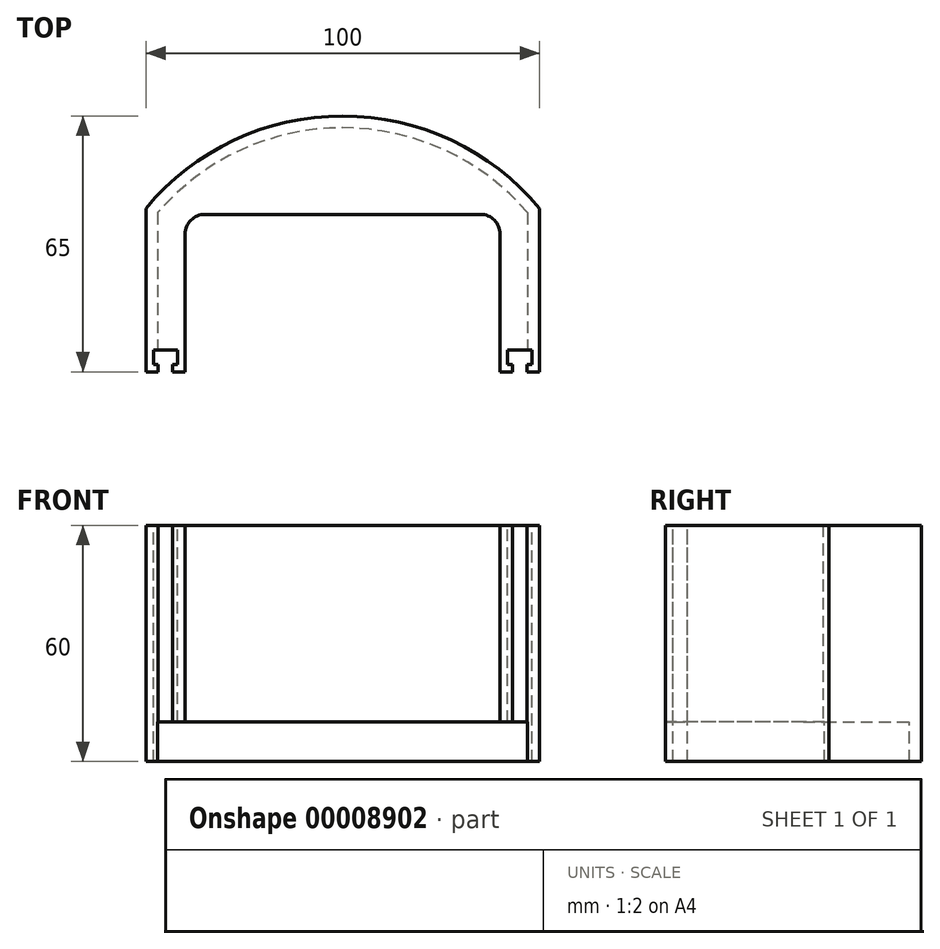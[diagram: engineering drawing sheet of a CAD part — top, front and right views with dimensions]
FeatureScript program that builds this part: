
annotation { "Feature Type Name" : "Feature", "Feature Type Description" : "" }
export const myFeature = defineFeature(function(context is Context, id is Id, definition is map)
    precondition{}
    {
        {
            var Q0;
            Q0=qCreatedBy(makeId("Top.planeOp"),FACE);
            var sketch = newSketch(context, id + "F0", { "sketchPlane" : qUnion([Q0])});
            skLineSegment(sketch, "E0", {"start": v(0, 0) * mm, "end": v(-40, 0) * mm});
            skLineSegment(sketch, "E1", {"start": v(0, 0) * mm, "end": v(40, 0) * mm});
            skLineSegment(sketch, "E2", {"start": v(0, 35) * mm, "end": v(0, 0) * mm});
            skLineSegment(sketch, "E3", {"start": v(-40, 0) * mm, "end": v(-43.59, 0) * mm});
            skLineSegment(sketch, "E4", {"start": v(40, 0) * mm, "end": v(43.59, 0) * mm});
            skLineSegment(sketch, "E5", {"start": v(-43.59, 0) * mm, "end": v(-50, 0) * mm});
            skLineSegment(sketch, "E6", {"start": v(43.59, 0) * mm, "end": v(50, 0) * mm});
            skCircle(sketch, "E7.0", {"center": v(0, 0) * mm, "radius": 65 * mm});
            skLineSegment(sketch, "E8.0", {"start": v(40, 35) * mm, "end": v(40, 0) * mm});
            skLineSegment(sketch, "E9.0", {"start": v(-40, 35) * mm, "end": v(-40, 0) * mm});
            skLineSegment(sketch, "E10.0", {"start": v(0, 40) * mm, "end": v(-35, 40) * mm});
            skLineSegment(sketch, "E10.1", {"start": v(0, 40) * mm, "end": v(35, 40) * mm});
            skPoint(sketch, "E11.visualSharp", {"position": v(-40, 40) * mm});
            skArc(sketch, "E11.filletArc", {"start": v(-35, 40) * mm, "mid": v(-38.54, 38.54) * mm, "end": v(-40, 35) * mm});
            skPoint(sketch, "E12.visualSharp", {"position": v(40, 40) * mm});
            skArc(sketch, "E12.filletArc", {"start": v(40, 35) * mm, "mid": v(38.54, 38.54) * mm, "end": v(35, 40) * mm});
            skLineSegment(sketch, "E13.0", {"start": v(-50, 41.53) * mm, "end": v(-50, 0) * mm});
            skLineSegment(sketch, "E14.0", {"start": v(50, 41.53) * mm, "end": v(50, 0) * mm});
            skSolve(sketch);
        }
        {
            var Q0;
            Q0=makeQuery(id+"F0.imprint","IMPRINT",FACE,{"disambiguationData":[TD([[makeQuery(id+"F0.imprint","IMPRINT",EDGE,{"derivedFrom":sQuery(id+"F0.wireOp",EDGE,"E3")}),-1.0]])]});
            extrude(context, id + "F1", {"entities" : qUnion([Q0]), "depth" : 50 * mm});
        }
        {
            var Q0;
            Q0=makeQuery(id+"F1.opExtrude","CAP_FACE",FACE,{"disambiguationData":[OSD([sQuery(id+"F0.wireOp",EDGE,"E3"),sQuery(id+"F0.wireOp",EDGE,"E4"),sQuery(id+"F0.wireOp",EDGE,"E5"),sQuery(id+"F0.wireOp",EDGE,"E6"),sQuery(id+"F0.wireOp",EDGE,"E7.0"),sQuery(id+"F0.wireOp",EDGE,"E8.0"),sQuery(id+"F0.wireOp",EDGE,"E9.0"),sQuery(id+"F0.wireOp",EDGE,"E10.0"),sQuery(id+"F0.wireOp",EDGE,"E10.1"),sQuery(id+"F0.wireOp",EDGE,"E11.filletArc"),sQuery(id+"F0.wireOp",EDGE,"E12.filletArc"),sQuery(id+"F0.wireOp",EDGE,"E13.0"),sQuery(id+"F0.wireOp",EDGE,"E14.0")])],"isStart":false});
            var sketch = newSketch(context, id + "F2", { "sketchPlane" : qUnion([Q0])});
            skLineSegment(sketch, "E15.0", {"start": v(35, 32.9) * mm, "end": v(35, 0) * mm});
            skLineSegment(sketch, "E16", {"start": v(-50, 0) * mm, "end": v(-50, 5) * mm});
            skLineSegment(sketch, "E17.0", {"start": v(-43.75, 0) * mm, "end": v(-43.75, 2.5) * mm, "construction": true});
            skLineSegment(sketch, "E18.0", {"start": v(-46.25, 0) * mm, "end": v(-46.25, 2.5) * mm, "construction": true});
            skLineSegment(sketch, "E19.0", {"start": v(-47.5, 2.5) * mm, "end": v(-47.5, 5) * mm, "construction": true});
            skLineSegment(sketch, "E20.0", {"start": v(-42.5, 2.5) * mm, "end": v(-42.5, 5) * mm, "construction": true});
            skLineSegment(sketch, "E21", {"start": v(-47.5, 5) * mm, "end": v(-42.5, 5) * mm, "construction": true});
            skLineSegment(sketch, "E22.0", {"start": v(-47.5, 2.5) * mm, "end": v(-46.25, 2.5) * mm, "construction": true});
            skLineSegment(sketch, "E23.trimOffspring", {"start": v(-43.75, 2.5) * mm, "end": v(-42.5, 2.5) * mm, "construction": true});
            skLineSegment(sketch, "E24.0", {"start": v(-48.1, 1.9) * mm, "end": v(-48.1, 5.6) * mm});
            skLineSegment(sketch, "E25.0", {"start": v(-48.1, 5.6) * mm, "end": v(-41.9, 5.6) * mm});
            skLineSegment(sketch, "E26.0", {"start": v(-41.9, 1.9) * mm, "end": v(-41.9, 5.6) * mm});
            skLineSegment(sketch, "E27.0", {"start": v(-48.1, 1.9) * mm, "end": v(-46.85, 1.9) * mm});
            skLineSegment(sketch, "E28.0", {"start": v(-43.15, 1.9) * mm, "end": v(-41.9, 1.9) * mm});
            skLineSegment(sketch, "E29.0", {"start": v(-46.85, 0) * mm, "end": v(-46.85, 1.9) * mm});
            skLineSegment(sketch, "E30.0", {"start": v(-43.15, 0) * mm, "end": v(-43.15, 1.9) * mm});
            skLineSegment(sketch, "E31", {"start": v(50, 0) * mm, "end": v(50, 5) * mm});
            skLineSegment(sketch, "E32.0", {"start": v(46.25, 0) * mm, "end": v(46.25, 2.5) * mm, "construction": true});
            skLineSegment(sketch, "E33.0", {"start": v(47.5, 2.5) * mm, "end": v(47.5, 5) * mm, "construction": true});
            skLineSegment(sketch, "E34.0", {"start": v(43.75, 0) * mm, "end": v(43.75, 2.5) * mm, "construction": true});
            skLineSegment(sketch, "E35.0", {"start": v(42.5, 2.5) * mm, "end": v(42.5, 5) * mm, "construction": true});
            skLineSegment(sketch, "E36", {"start": v(47.5, 5) * mm, "end": v(42.5, 5) * mm, "construction": true});
            skLineSegment(sketch, "E37.0", {"start": v(47.5, 2.5) * mm, "end": v(46.25, 2.5) * mm, "construction": true});
            skLineSegment(sketch, "E38.trimOffspring", {"start": v(43.75, 2.5) * mm, "end": v(42.5, 2.5) * mm, "construction": true});
            skLineSegment(sketch, "E39.0", {"start": v(48.1, 5.6) * mm, "end": v(41.9, 5.6) * mm});
            skLineSegment(sketch, "E40.0", {"start": v(48.1, 1.9) * mm, "end": v(48.1, 5.6) * mm});
            skLineSegment(sketch, "E41.0", {"start": v(41.9, 1.9) * mm, "end": v(41.9, 5.6) * mm});
            skLineSegment(sketch, "E42.0", {"start": v(43.15, 0) * mm, "end": v(43.15, 1.9) * mm});
            skLineSegment(sketch, "E43.0", {"start": v(46.85, 0) * mm, "end": v(46.85, 1.9) * mm});
            skLineSegment(sketch, "E44.0", {"start": v(48.1, 1.9) * mm, "end": v(46.85, 1.9) * mm});
            skLineSegment(sketch, "E45.0", {"start": v(43.15, 1.9) * mm, "end": v(41.9, 1.9) * mm});
            skSolve(sketch);
        }
        {
            var Q0;
            Q0=makeQuery(id+"F2.imprint","IMPRINT",FACE,{"disambiguationData":[TD([[makeQuery(id+"F2.imprint","IMPRINT",EDGE,{"derivedFrom":sQuery(id+"F2.wireOp",EDGE,"E39.0")}),1.0]])]});
            var Q1;
            Q1=makeQuery(id+"F2.imprint","IMPRINT",FACE,{"disambiguationData":[TD([[makeQuery(id+"F2.imprint","IMPRINT",EDGE,{"derivedFrom":sQuery(id+"F2.wireOp",EDGE,"E24.0")}),-1.0]])]});
            extrude(context, id + "F3", {"entities" : qUnion([Q0, Q1]), "operationType" : NewBodyOperationType.REMOVE, "oppositeDirection" : true, "depth" : 190 * mm});
        }
        {
            var Q0;
            Q0=makeQuery(id+"F1.opExtrude","CAP_FACE",FACE,{"disambiguationData":[OSD([sQuery(id+"F0.wireOp",EDGE,"E3"),sQuery(id+"F0.wireOp",EDGE,"E4"),sQuery(id+"F0.wireOp",EDGE,"E5"),sQuery(id+"F0.wireOp",EDGE,"E6"),sQuery(id+"F0.wireOp",EDGE,"E7.0"),sQuery(id+"F0.wireOp",EDGE,"E8.0"),sQuery(id+"F0.wireOp",EDGE,"E9.0"),sQuery(id+"F0.wireOp",EDGE,"E10.0"),sQuery(id+"F0.wireOp",EDGE,"E10.1"),sQuery(id+"F0.wireOp",EDGE,"E11.filletArc"),sQuery(id+"F0.wireOp",EDGE,"E12.filletArc"),sQuery(id+"F0.wireOp",EDGE,"E13.0"),sQuery(id+"F0.wireOp",EDGE,"E14.0")])],"isStart":true});
            var sketch = newSketch(context, id + "F4", { "sketchPlane" : qUnion([Q0])});
            skLineSegment(sketch, "E46.0", {"start": v(-48.1, -10.6) * mm, "end": v(-41.9, -10.6) * mm});
            skLineSegment(sketch, "E47.0", {"start": v(48.1, -10.6) * mm, "end": v(41.9, -10.6) * mm});
            skLineSegment(sketch, "E48.0", {"start": v(-47, -40.44) * mm, "end": v(-47, 0) * mm});
            skArc(sketch, "E48.1", {"start": v(47, -40.44) * mm, "mid": v(0, -62) * mm, "end": v(-47, -40.44) * mm});
            skLineSegment(sketch, "E48.2", {"start": v(47, -40.44) * mm, "end": v(47, 0) * mm});
            skLineSegment(sketch, "E49.0", {"start": v(-43, -35) * mm, "end": v(-43, 0) * mm});
            skArc(sketch, "E49.1", {"start": v(-35, -43) * mm, "mid": v(-40.66, -40.66) * mm, "end": v(-43, -35) * mm});
            skLineSegment(sketch, "E49.2", {"start": v(35, -43) * mm, "end": v(-35, -43) * mm});
            skArc(sketch, "E49.3", {"start": v(43, -35) * mm, "mid": v(40.66, -40.66) * mm, "end": v(35, -43) * mm});
            skLineSegment(sketch, "E49.4", {"start": v(43, -35) * mm, "end": v(43, 0) * mm});
            skSolve(sketch);
        }
        {
            var Q0;
            {var subQ10=sQuery(id+"F4.wireOp",EDGE,"E48.1");Q0=makeQuery(id+"F4.imprint","IMPRINT",FACE,{"disambiguationData":[TD([[makeQuery(id+"F4.imprint","IMPRINT",EDGE,{"derivedFrom":subQ10}),-1.0]])]});}
            extrude(context, id + "F5", {"entities" : qUnion([Q0]), "operationType" : NewBodyOperationType.ADD, "depth" : 10 * mm});
        }
    });
